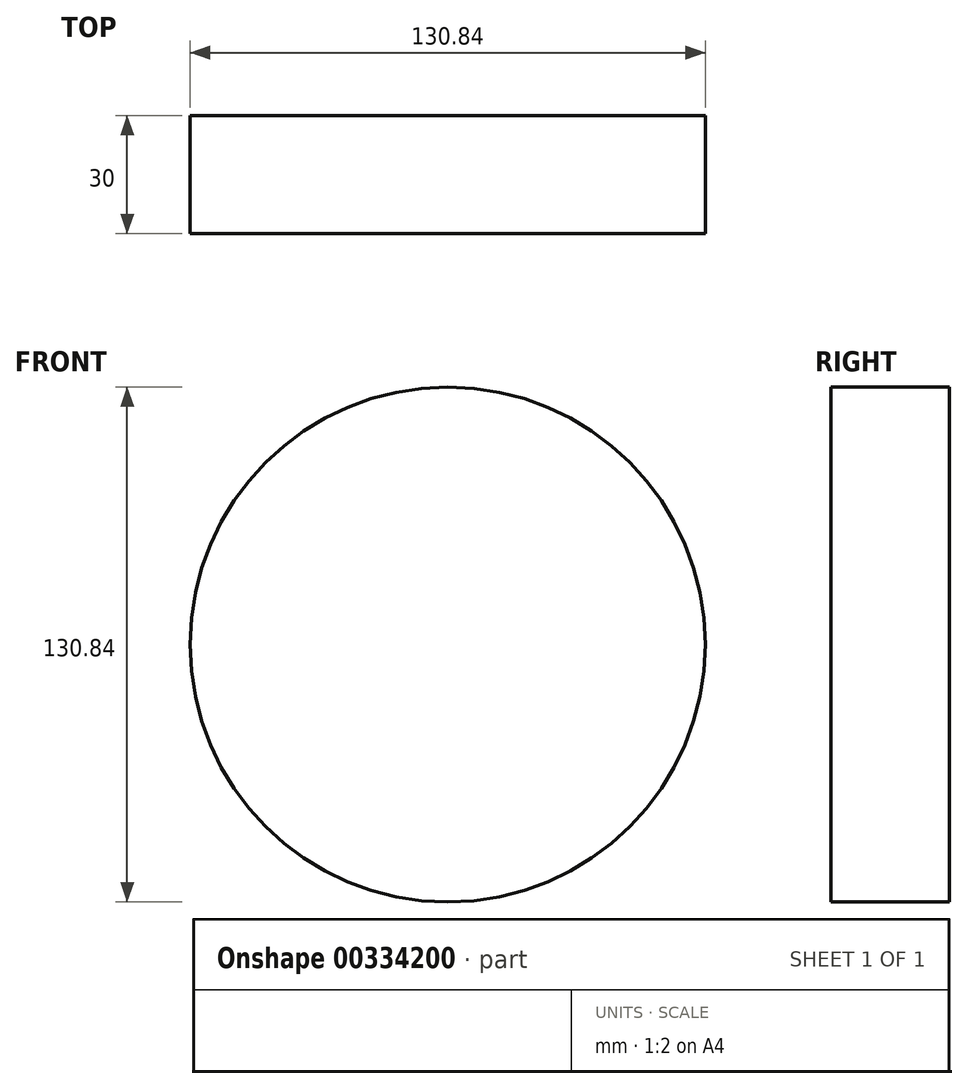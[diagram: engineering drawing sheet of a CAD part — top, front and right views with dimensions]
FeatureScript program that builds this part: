
annotation { "Feature Type Name" : "Feature", "Feature Type Description" : "" }
export const myFeature = defineFeature(function(context is Context, id is Id, definition is map)
    precondition{}
    {
        {
            var Q0;
            Q0=qCreatedBy(makeId("Front.planeOp"),FACE);
            var sketch = newSketch(context, id + "F0", { "sketchPlane" : qUnion([Q0])});
            skCircle(sketch, "E0", {"center": v(0, 0) * mm, "radius": 65.42 * mm});
            skSolve(sketch);
        }
        {
            var Q0;
            Q0=makeQuery(id+"F0.imprint","IMPRINT",FACE,{"disambiguationData":[TD([[makeQuery(id+"F0.imprint","IMPRINT",EDGE,{"derivedFrom":sQuery(id+"F0.wireOp",EDGE,"E0")}),1.0]])]});
            extrude(context, id + "F1", {"entities" : qUnion([Q0]), "depth" : 30 * mm});
        }
    });
